# Revit family: SmartVide_9_GENERADO
name_source: partatom
category: Equipos especializados
revit_build: Autodesk Revit 2016 (Build: 20151007_0715(x64)
units: mm (PartAtom-declared; Revit-internal decimal feet)

## family parameters
Compartido = No
Corte con vacíos al cargar = No
Cota de conector redondo = Diámetro de uso
Número OmniClass = 23.21.21.13
Punto de cálculo de habitación = No
Se basa en plano de trabajo = No
Siempre vertical = Sí
Tipo de pieza = Normal

## types (3) — shared parameters
Comentarios de tipo = Max. capacity: 56 lt./14 gal.
Cycle = 50 Hz
Depth = 140 mm  [stored 0.459318 ft]
Fabricante = SAMMIC S.L.
Foodservice Equipment Identifier = Sí
Height = 360 mm  [stored 1.1811 ft]
Phase = 1
Revision Code = 1
Specification by Manufacturer = Commercial high-precision sous-vide cooker. Reliable, user-friendly, portable.
Interchangeable between ºC and ºF.
· Bluetooth connectivity.
· HACCP-ready.
· Optional core probe.
· Firmware update.
URL = https://www.sammic.com
URL Cutsheet = http://www.sammic.com
Weight in Pounds = 9.3
Width = 124 mm  [stored 0.406824 ft]

## per-type parameters (varying)
| type | Electric Connection Type | FL Amps | Modelo | Volts |
| SmartVide 9 230/50-60/1 UK | UK | 8 A | 1180141 | 230 V |
| SmartVide 9 120/60/1 | USA | 12 A | 1180143 | 120 V |
| SmartVide 9 230/50-60/1 | EU | 8 A | 1180140 | 230 V |

note: column(s) folded — value = type name in every type: Descripción

note: [stored X ft] marks values corroborated as IEEE doubles in the binary element streams (Revit-internal decimal feet)
